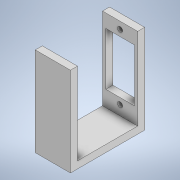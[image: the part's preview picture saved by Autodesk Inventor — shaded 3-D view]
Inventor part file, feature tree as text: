
AUTODESK INVENTOR PART (.ipt)
format: ipt  version: 2020.3 (Build 243373000, 373)  size: 140,800 bytes
history: native  units: mm
features: extrude x3, sketch x3
ambient origin geometry x8: Origin, YZ Plane, XZ Plane, XY Plane, X Axis, Y Axis, Z Axis, Center Point
bodies: Solid1 (feature_tree)
feature tree (6):
  extrude  "Extrusion1"  Depth=3.0mm
  extrude  "Extrusion2"  Depth=35.0mm TaperAngle=0.0deg
  extrude  "Extrusion3"  Depth=10.0mm TaperAngle=0.0deg
  sketch  "Sketch1"  dims[d3=3.0mm d4=0.0mm d5=3.0mm]
  sketch  "Sketch2"  dims[d6=3.0mm d7=35.0mm d8=0.0mm]
  sketch  "Sketch4"  dims[d9=2.0mm d10=10.0mm d11=0.0mm]
